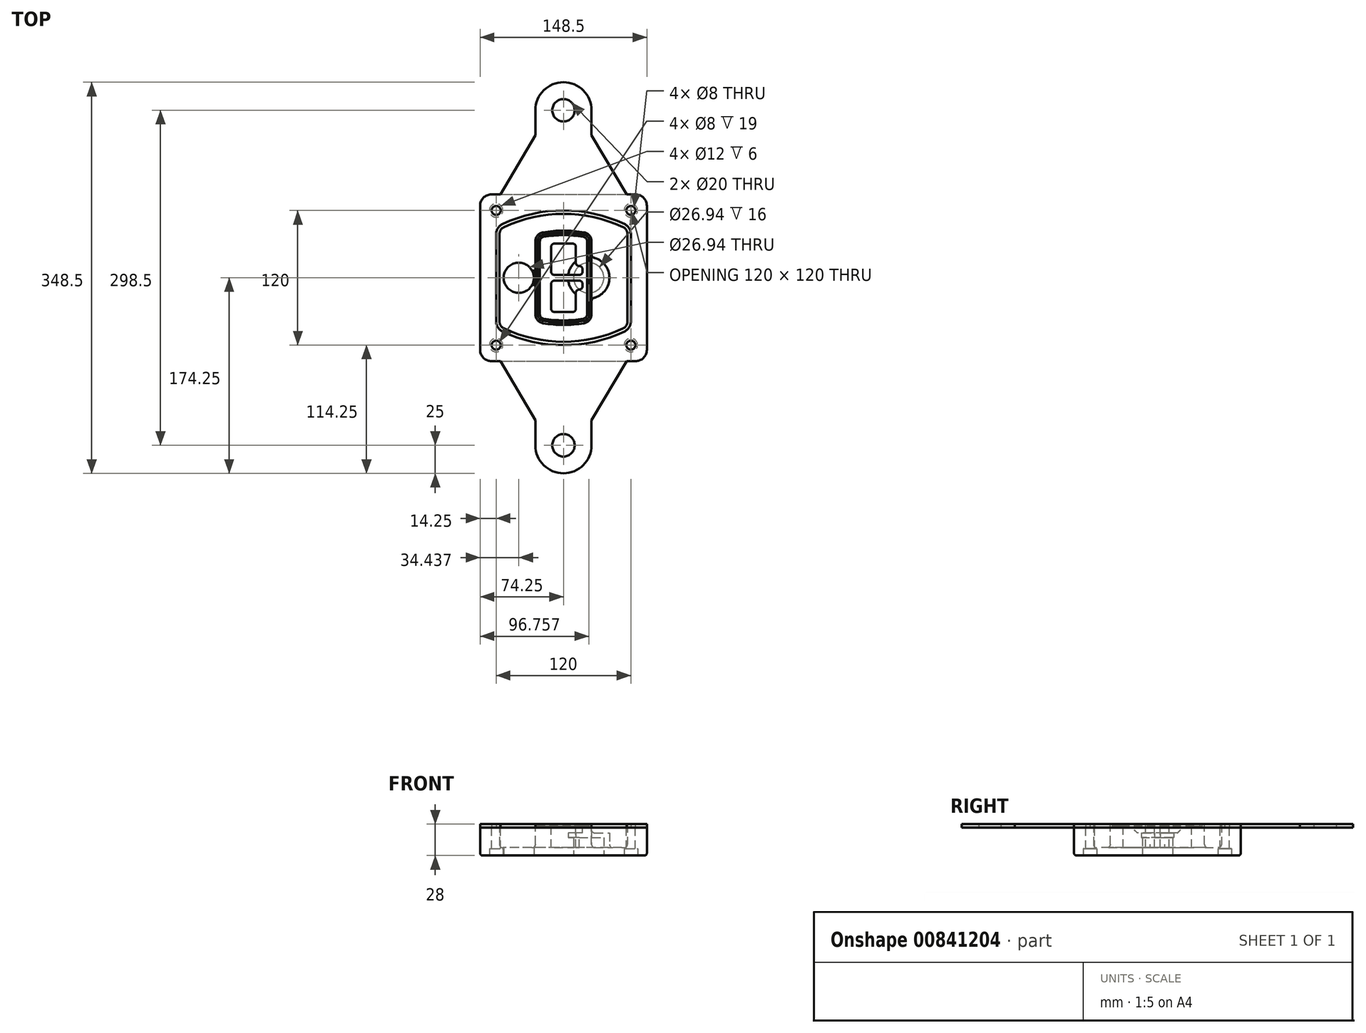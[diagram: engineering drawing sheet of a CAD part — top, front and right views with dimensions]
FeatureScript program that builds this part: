
annotation { "Feature Type Name" : "Feature", "Feature Type Description" : "" }
export const myFeature = defineFeature(function(context is Context, id is Id, definition is map)
    precondition{}
    {
        {
            var Q0;
            Q0=qCreatedBy(makeId("Top.planeOp"),FACE);
            var sketch = newSketch(context, id + "F0", { "sketchPlane" : qUnion([Q0])});
            skPoint(sketch, "E0.rect.middle", {"position": v(0, 0) * mm});
            skLineSegment(sketch, "E1.bottom", {"start": v(-64.25, -74.25) * mm, "end": v(64.25, -74.25) * mm});
            skLineSegment(sketch, "E1.top", {"start": v(-64.25, 74.25) * mm, "end": v(64.25, 74.25) * mm});
            skLineSegment(sketch, "E1.left", {"start": v(-74.25, -64.25) * mm, "end": v(-74.25, 64.25) * mm});
            skLineSegment(sketch, "E1.right", {"start": v(74.25, -64.25) * mm, "end": v(74.25, 64.25) * mm});
            skLineSegment(sketch, "E2", {"start": v(-74.25, 74.25) * mm, "end": v(74.25, -74.25) * mm, "construction": true});
            skLineSegment(sketch, "E3", {"start": v(74.25, 74.25) * mm, "end": v(-74.25, -74.25) * mm, "construction": true});
            skCircle(sketch, "E4", {"center": v(-60, 60) * mm, "radius": 4 * mm});
            skCircle(sketch, "E5", {"center": v(60, 60) * mm, "radius": 4 * mm});
            skCircle(sketch, "E6", {"center": v(60, -60) * mm, "radius": 4 * mm});
            skCircle(sketch, "E7", {"center": v(-60, -60) * mm, "radius": 4 * mm});
            skLineSegment(sketch, "E8", {"start": v(-60, 60) * mm, "end": v(60, 60) * mm, "construction": true});
            skLineSegment(sketch, "E9", {"start": v(60, 60) * mm, "end": v(60, -60) * mm, "construction": true});
            skLineSegment(sketch, "E10", {"start": v(60, -60) * mm, "end": v(-60, -60) * mm, "construction": true});
            skLineSegment(sketch, "E11", {"start": v(-60, -60) * mm, "end": v(-60, 60) * mm, "construction": true});
            skLineSegment(sketch, "E12", {"start": v(-60, 38.83) * mm, "end": v(-60, -38.83) * mm});
            skLineSegment(sketch, "E13", {"start": v(60, 38.83) * mm, "end": v(60, -38.83) * mm});
            skArc(sketch, "E14", {"start": v(54.26, 47.88) * mm, "mid": v(0, 60) * mm, "end": v(-54.26, 47.88) * mm});
            skArc(sketch, "E15", {"start": v(-54.26, -47.88) * mm, "mid": v(0, -60) * mm, "end": v(54.26, -47.88) * mm});
            skLineSegment(sketch, "E16", {"start": v(-60, 0) * mm, "end": v(60, 0) * mm, "construction": true});
            skPoint(sketch, "E17.visualSharp", {"position": v(-60, -45) * mm});
            skArc(sketch, "E17.filletArc", {"start": v(-60, -38.83) * mm, "mid": v(-58.44, -44.2) * mm, "end": v(-54.26, -47.88) * mm});
            skPoint(sketch, "E18.visualSharp", {"position": v(-60, 45) * mm});
            skArc(sketch, "E18.filletArc", {"start": v(-54.26, 47.88) * mm, "mid": v(-58.44, 44.2) * mm, "end": v(-60, 38.83) * mm});
            skPoint(sketch, "E19.visualSharp", {"position": v(60, 45) * mm});
            skArc(sketch, "E19.filletArc", {"start": v(60, 38.83) * mm, "mid": v(58.44, 44.2) * mm, "end": v(54.26, 47.88) * mm});
            skPoint(sketch, "E20.visualSharp", {"position": v(60, -45) * mm});
            skArc(sketch, "E20.filletArc", {"start": v(54.26, -47.88) * mm, "mid": v(58.44, -44.2) * mm, "end": v(60, -38.83) * mm});
            skPoint(sketch, "E21.visualSharp", {"position": v(-74.25, 74.25) * mm});
            skArc(sketch, "E21.filletArc", {"start": v(-64.25, 74.25) * mm, "mid": v(-71.32, 71.32) * mm, "end": v(-74.25, 64.25) * mm});
            skPoint(sketch, "E22.visualSharp", {"position": v(74.25, 74.25) * mm});
            skArc(sketch, "E22.filletArc", {"start": v(74.25, 64.25) * mm, "mid": v(71.32, 71.32) * mm, "end": v(64.25, 74.25) * mm});
            skPoint(sketch, "E23.visualSharp", {"position": v(74.25, -74.25) * mm});
            skArc(sketch, "E23.filletArc", {"start": v(64.25, -74.25) * mm, "mid": v(71.32, -71.32) * mm, "end": v(74.25, -64.25) * mm});
            skPoint(sketch, "E24.visualSharp", {"position": v(-74.25, -74.25) * mm});
            skArc(sketch, "E24.filletArc", {"start": v(-74.25, -64.25) * mm, "mid": v(-71.32, -71.32) * mm, "end": v(-64.25, -74.25) * mm});
            skArc(sketch, "E25.0", {"start": v(57, 38.83) * mm, "mid": v(55.9, 42.58) * mm, "end": v(52.98, 45.17) * mm});
            skLineSegment(sketch, "E25.1", {"start": v(57, 38.83) * mm, "end": v(57, -38.83) * mm});
            skArc(sketch, "E25.2", {"start": v(52.98, -45.17) * mm, "mid": v(55.9, -42.58) * mm, "end": v(57, -38.83) * mm});
            skArc(sketch, "E25.3", {"start": v(-52.98, -45.17) * mm, "mid": v(0, -57) * mm, "end": v(52.98, -45.17) * mm});
            skArc(sketch, "E25.4", {"start": v(-57, -38.83) * mm, "mid": v(-55.9, -42.58) * mm, "end": v(-52.98, -45.17) * mm});
            skArc(sketch, "E25.5", {"start": v(52.98, 45.17) * mm, "mid": v(0, 57) * mm, "end": v(-52.98, 45.17) * mm});
            skLineSegment(sketch, "E25.6", {"start": v(-57, 38.83) * mm, "end": v(-57, -38.83) * mm});
            skArc(sketch, "E25.7", {"start": v(-52.98, 45.17) * mm, "mid": v(-55.9, 42.58) * mm, "end": v(-57, 38.83) * mm});
            skArc(sketch, "E26.0", {"start": v(-55.96, 51.5) * mm, "mid": v(-61.82, 46.33) * mm, "end": v(-64, 38.83) * mm});
            skArc(sketch, "E26.1", {"start": v(55.96, 51.5) * mm, "mid": v(0, 64) * mm, "end": v(-55.96, 51.5) * mm});
            skArc(sketch, "E26.2", {"start": v(64, 38.83) * mm, "mid": v(61.82, 46.33) * mm, "end": v(55.96, 51.5) * mm});
            skLineSegment(sketch, "E26.3", {"start": v(64, 38.83) * mm, "end": v(64, -38.83) * mm});
            skArc(sketch, "E26.4", {"start": v(55.96, -51.5) * mm, "mid": v(61.82, -46.33) * mm, "end": v(64, -38.83) * mm});
            skLineSegment(sketch, "E26.5", {"start": v(-64, 38.83) * mm, "end": v(-64, -38.83) * mm});
            skArc(sketch, "E26.6", {"start": v(-55.96, -51.5) * mm, "mid": v(0, -64) * mm, "end": v(55.96, -51.5) * mm});
            skArc(sketch, "E26.7", {"start": v(-64, -38.83) * mm, "mid": v(-61.82, -46.33) * mm, "end": v(-55.96, -51.5) * mm});
            skSolve(sketch);
        }
        {
            var Q0;
            Q0=makeQuery(id+"F0.imprint","IMPRINT",FACE,{"disambiguationData":[TD([[makeQuery(id+"F0.imprint","IMPRINT",EDGE,{"derivedFrom":sQuery(id+"F0.wireOp",EDGE,"E1.bottom")}),1.0]])]});
            var Q1;
            Q1=makeQuery(id+"F0.imprint","IMPRINT",FACE,{"disambiguationData":[TD([[makeQuery(id+"F0.imprint","IMPRINT",EDGE,{"derivedFrom":sQuery(id+"F0.wireOp",EDGE,"E12")}),1.0]])]});
            var Q2;
            Q2=makeQuery(id+"F0.imprint","IMPRINT",FACE,{"disambiguationData":[TD([[makeQuery(id+"F0.imprint","IMPRINT",EDGE,{"derivedFrom":sQuery(id+"F0.wireOp",EDGE,"E25.0")}),1.0]])]});
            var Q3;
            Q3=makeQuery(id+"F0.imprint","IMPRINT",FACE,{"disambiguationData":[TD([[makeQuery(id+"F0.imprint","IMPRINT",EDGE,{"derivedFrom":sQuery(id+"F0.wireOp",EDGE,"E12")}),-1.0]])]});
            extrude(context, id + "F1", {"entities" : qUnion([Q0, Q1, Q2, Q3]), "oppositeDirection" : true, "depth" : 25 * mm});
        }
        {
            var Q0;
            Q0=makeQuery(id+"F0.imprint","IMPRINT",FACE,{"disambiguationData":[TD([[makeQuery(id+"F0.imprint","IMPRINT",EDGE,{"derivedFrom":sQuery(id+"F0.wireOp",EDGE,"E12")}),1.0]])]});
            extrude(context, id + "F2", {"entities" : qUnion([Q0]), "operationType" : NewBodyOperationType.ADD, "depth" : 3 * mm});
        }
        {
            var Q0;
            Q0=makeQuery(id+"F0.imprint","IMPRINT",FACE,{"disambiguationData":[TD([[makeQuery(id+"F0.imprint","IMPRINT",EDGE,{"derivedFrom":sQuery(id+"F0.wireOp",EDGE,"E25.0")}),1.0]])]});
            extrude(context, id + "F3", {"entities" : qUnion([Q0]), "operationType" : NewBodyOperationType.REMOVE, "oppositeDirection" : true, "depth" : 18 * mm});
        }
        {
            var Q0;
            Q0=makeQuery(id+"F2.opExtrude","CAP_FACE",FACE,{"disambiguationData":[OSD([sQuery(id+"F0.wireOp",EDGE,"E12"),sQuery(id+"F0.wireOp",EDGE,"E13"),sQuery(id+"F0.wireOp",EDGE,"E14"),sQuery(id+"F0.wireOp",EDGE,"E15"),sQuery(id+"F0.wireOp",EDGE,"E17.filletArc"),sQuery(id+"F0.wireOp",EDGE,"E18.filletArc"),sQuery(id+"F0.wireOp",EDGE,"E19.filletArc"),sQuery(id+"F0.wireOp",EDGE,"E20.filletArc"),sQuery(id+"F0.wireOp",EDGE,"E25.0"),sQuery(id+"F0.wireOp",EDGE,"E25.1"),sQuery(id+"F0.wireOp",EDGE,"E25.2"),sQuery(id+"F0.wireOp",EDGE,"E25.3"),sQuery(id+"F0.wireOp",EDGE,"E25.4"),sQuery(id+"F0.wireOp",EDGE,"E25.5"),sQuery(id+"F0.wireOp",EDGE,"E25.6"),sQuery(id+"F0.wireOp",EDGE,"E25.7")])],"isStart":false});
            var sketch = newSketch(context, id + "F4", { "sketchPlane" : qUnion([Q0])});
            skArc(sketch, "E27.0", {"start": v(-18.34, -40.45) * mm, "mid": v(0, -42) * mm, "end": v(18.34, -40.45) * mm});
            skArc(sketch, "E28.0", {"start": v(18.34, 40.45) * mm, "mid": v(0, 42) * mm, "end": v(-18.34, 40.45) * mm});
            skLineSegment(sketch, "E29", {"start": v(-25, 32.57) * mm, "end": v(-25, -32.57) * mm});
            skLineSegment(sketch, "E30", {"start": v(25, 32.57) * mm, "end": v(25, -32.57) * mm});
            skLineSegment(sketch, "E31", {"start": v(-25, 39.1) * mm, "end": v(25, 39.1) * mm, "construction": true});
            skLineSegment(sketch, "E32", {"start": v(-25, -39.1) * mm, "end": v(25, -39.1) * mm, "construction": true});
            skPoint(sketch, "E33.visualSharp", {"position": v(-25, 39.1) * mm});
            skArc(sketch, "E33.filletArc", {"start": v(-18.34, 40.45) * mm, "mid": v(-23.11, 37.73) * mm, "end": v(-25, 32.57) * mm});
            skPoint(sketch, "E34.visualSharp", {"position": v(25, 39.1) * mm});
            skArc(sketch, "E34.filletArc", {"start": v(25, 32.57) * mm, "mid": v(23.11, 37.73) * mm, "end": v(18.34, 40.45) * mm});
            skPoint(sketch, "E35.visualSharp", {"position": v(25, -39.1) * mm});
            skArc(sketch, "E35.filletArc", {"start": v(18.34, -40.45) * mm, "mid": v(23.11, -37.73) * mm, "end": v(25, -32.57) * mm});
            skPoint(sketch, "E36.visualSharp", {"position": v(-25, -39.1) * mm});
            skArc(sketch, "E36.filletArc", {"start": v(-25, -32.57) * mm, "mid": v(-23.11, -37.73) * mm, "end": v(-18.34, -40.45) * mm});
            skArc(sketch, "E37.0", {"start": v(52.98, 45.17) * mm, "mid": v(0, 57) * mm, "end": v(-52.98, 45.17) * mm});
            skArc(sketch, "E37.1", {"start": v(-52.98, 45.17) * mm, "mid": v(-55.9, 42.58) * mm, "end": v(-57, 38.83) * mm});
            skLineSegment(sketch, "E37.2", {"start": v(-57, 38.83) * mm, "end": v(-57, -38.83) * mm});
            skArc(sketch, "E37.3", {"start": v(-57, -38.83) * mm, "mid": v(-55.9, -42.58) * mm, "end": v(-52.98, -45.17) * mm});
            skArc(sketch, "E37.4", {"start": v(-52.98, -45.17) * mm, "mid": v(0, -57) * mm, "end": v(52.98, -45.17) * mm});
            skArc(sketch, "E37.5", {"start": v(52.98, -45.17) * mm, "mid": v(55.9, -42.58) * mm, "end": v(57, -38.83) * mm});
            skLineSegment(sketch, "E37.6", {"start": v(57, 38.83) * mm, "end": v(57, -38.83) * mm});
            skArc(sketch, "E37.7", {"start": v(57, 38.83) * mm, "mid": v(55.9, 42.58) * mm, "end": v(52.98, 45.17) * mm});
            skLineSegment(sketch, "E38.0", {"start": v(23, 32.57) * mm, "end": v(23, -32.57) * mm});
            skArc(sketch, "E38.1", {"start": v(18, -38.48) * mm, "mid": v(21.58, -36.44) * mm, "end": v(23, -32.57) * mm});
            skArc(sketch, "E38.2", {"start": v(-18, -38.48) * mm, "mid": v(0, -40) * mm, "end": v(18, -38.48) * mm});
            skArc(sketch, "E38.3", {"start": v(-23, -32.57) * mm, "mid": v(-21.58, -36.44) * mm, "end": v(-18, -38.48) * mm});
            skLineSegment(sketch, "E38.4", {"start": v(-23, 32.57) * mm, "end": v(-23, -32.57) * mm});
            skArc(sketch, "E38.5", {"start": v(23, 32.57) * mm, "mid": v(21.58, 36.44) * mm, "end": v(18, 38.48) * mm});
            skArc(sketch, "E38.6", {"start": v(-18, 38.48) * mm, "mid": v(-21.58, 36.44) * mm, "end": v(-23, 32.57) * mm});
            skArc(sketch, "E38.7", {"start": v(18, 38.48) * mm, "mid": v(0, 40) * mm, "end": v(-18, 38.48) * mm});
            skArc(sketch, "E39.0", {"start": v(21, 32.57) * mm, "mid": v(20.06, 35.15) * mm, "end": v(17.67, 36.5) * mm});
            skLineSegment(sketch, "E39.1", {"start": v(21, 32.57) * mm, "end": v(21, -32.57) * mm});
            skArc(sketch, "E39.2", {"start": v(17.67, -36.5) * mm, "mid": v(20.06, -35.15) * mm, "end": v(21, -32.57) * mm});
            skArc(sketch, "E39.3", {"start": v(-17.67, -36.5) * mm, "mid": v(0, -38) * mm, "end": v(17.67, -36.5) * mm});
            skArc(sketch, "E39.4", {"start": v(-21, -32.57) * mm, "mid": v(-20.06, -35.15) * mm, "end": v(-17.67, -36.5) * mm});
            skArc(sketch, "E39.5", {"start": v(17.67, 36.5) * mm, "mid": v(0, 38) * mm, "end": v(-17.67, 36.5) * mm});
            skLineSegment(sketch, "E39.6", {"start": v(-21, 32.57) * mm, "end": v(-21, -32.57) * mm});
            skArc(sketch, "E39.7", {"start": v(-17.67, 36.5) * mm, "mid": v(-20.06, 35.15) * mm, "end": v(-21, 32.57) * mm});
            skLineSegment(sketch, "E40", {"start": v(-25, 0) * mm, "end": v(25, 0) * mm, "construction": true});
            skLineSegment(sketch, "E41", {"start": v(-11, 5.5) * mm, "end": v(-11, 27.5) * mm});
            skLineSegment(sketch, "E42", {"start": v(-8, 30.5) * mm, "end": v(8, 30.5) * mm});
            skLineSegment(sketch, "E43", {"start": v(11, 27.5) * mm, "end": v(11, 13.5) * mm});
            skLineSegment(sketch, "E44", {"start": v(14, 10.5) * mm, "end": v(14, 10.5) * mm});
            skLineSegment(sketch, "E45", {"start": v(17, 7.5) * mm, "end": v(17, 5.5) * mm});
            skLineSegment(sketch, "E46", {"start": v(14, 2.5) * mm, "end": v(-8, 2.5) * mm});
            skPoint(sketch, "E47.visualSharp", {"position": v(-11, 30.5) * mm});
            skArc(sketch, "E47.filletArc", {"start": v(-8, 30.5) * mm, "mid": v(-10.12, 29.62) * mm, "end": v(-11, 27.5) * mm});
            skPoint(sketch, "E48.visualSharp", {"position": v(11, 30.5) * mm});
            skArc(sketch, "E48.filletArc", {"start": v(11, 27.5) * mm, "mid": v(10.12, 29.62) * mm, "end": v(8, 30.5) * mm});
            skPoint(sketch, "E49.visualSharp", {"position": v(11, 10.5) * mm});
            skArc(sketch, "E49.filletArc", {"start": v(11, 13.5) * mm, "mid": v(11.88, 11.38) * mm, "end": v(14, 10.5) * mm});
            skPoint(sketch, "E50.visualSharp", {"position": v(17, 10.5) * mm});
            skArc(sketch, "E50.filletArc", {"start": v(17, 7.5) * mm, "mid": v(16.12, 9.62) * mm, "end": v(14, 10.5) * mm});
            skPoint(sketch, "E51.visualSharp", {"position": v(17, 2.5) * mm});
            skArc(sketch, "E51.filletArc", {"start": v(14, 2.5) * mm, "mid": v(16.12, 3.38) * mm, "end": v(17, 5.5) * mm});
            skPoint(sketch, "E52.visualSharp", {"position": v(-11, 2.5) * mm});
            skArc(sketch, "E52.filletArc", {"start": v(-11, 5.5) * mm, "mid": v(-10.12, 3.38) * mm, "end": v(-8, 2.5) * mm});
            skLineSegment(sketch, "E53.0.MirrorCS", {"start": v(14, -2.5) * mm, "end": v(-8, -2.5) * mm});
            skArc(sketch, "E54.0.MirrorCS", {"start": v(-11, -5.5) * mm, "mid": v(-10.12, -3.38) * mm, "end": v(-8, -2.5) * mm});
            skLineSegment(sketch, "E55.0.MirrorCS", {"start": v(-11, -5.5) * mm, "end": v(-11, -27.5) * mm});
            skArc(sketch, "E56.0.MirrorCS", {"start": v(-8, -30.5) * mm, "mid": v(-10.12, -29.62) * mm, "end": v(-11, -27.5) * mm});
            skLineSegment(sketch, "E57.0.MirrorCS", {"start": v(-8, -30.5) * mm, "end": v(8, -30.5) * mm});
            skArc(sketch, "E58.0.MirrorCS", {"start": v(11, -27.5) * mm, "mid": v(10.12, -29.62) * mm, "end": v(8, -30.5) * mm});
            skLineSegment(sketch, "E59.0.MirrorCS", {"start": v(11, -27.5) * mm, "end": v(11, -13.5) * mm});
            skArc(sketch, "E60.0.MirrorCS", {"start": v(11, -13.5) * mm, "mid": v(11.88, -11.38) * mm, "end": v(14, -10.5) * mm});
            skArc(sketch, "E61.0.MirrorCS", {"start": v(17, -7.5) * mm, "mid": v(16.12, -9.62) * mm, "end": v(14, -10.5) * mm});
            skLineSegment(sketch, "E62.0.MirrorCS", {"start": v(17, -7.5) * mm, "end": v(17, -5.5) * mm});
            skArc(sketch, "E63.0.MirrorCS", {"start": v(14, -2.5) * mm, "mid": v(16.12, -3.38) * mm, "end": v(17, -5.5) * mm});
            skSolve(sketch);
        }
        {
            var Q0;
            Q0=makeQuery(id+"F4.imprint","IMPRINT",FACE,{"disambiguationData":[TD([[makeQuery(id+"F4.imprint","IMPRINT",EDGE,{"derivedFrom":sQuery(id+"F4.wireOp",EDGE,"E27.0")}),1.0]])]});
            var Q1;
            Q1=makeQuery(id+"F4.imprint","IMPRINT",FACE,{"disambiguationData":[TD([[makeQuery(id+"F4.imprint","IMPRINT",EDGE,{"derivedFrom":sQuery(id+"F4.wireOp",EDGE,"E38.0")}),-1.0]])]});
            var Q2;
            Q2=makeQuery(id+"F4.imprint","IMPRINT",FACE,{"disambiguationData":[TD([[makeQuery(id+"F4.imprint","IMPRINT",EDGE,{"derivedFrom":sQuery(id+"F4.wireOp",EDGE,"E39.0")}),1.0]])]});
            extrude(context, id + "F5", {"entities" : qUnion([Q0, Q1, Q2]), "operationType" : NewBodyOperationType.ADD, "endBound" : BoundingType.UP_TO_NEXT, "oppositeDirection" : true, "depth" : 25 * mm});
        }
        {
            var Q0;
            Q0=makeQuery(id+"F4.imprint","IMPRINT",FACE,{"disambiguationData":[TD([[makeQuery(id+"F4.imprint","IMPRINT",EDGE,{"derivedFrom":sQuery(id+"F4.wireOp",EDGE,"E38.0")}),-1.0]])]});
            extrude(context, id + "F6", {"entities" : qUnion([Q0]), "operationType" : NewBodyOperationType.REMOVE, "oppositeDirection" : true, "depth" : 2 * mm});
        }
        {
            var Q0;
            Q0=makeQuery(id+"F1.opExtrude","CAP_FACE",FACE,{"disambiguationData":[OSD([sQuery(id+"F0.wireOp",EDGE,"E1.bottom"),sQuery(id+"F0.wireOp",EDGE,"E1.top"),sQuery(id+"F0.wireOp",EDGE,"E1.left"),sQuery(id+"F0.wireOp",EDGE,"E1.right"),sQuery(id+"F0.wireOp",EDGE,"E4"),sQuery(id+"F0.wireOp",EDGE,"E5"),sQuery(id+"F0.wireOp",EDGE,"E6"),sQuery(id+"F0.wireOp",EDGE,"E7"),sQuery(id+"F0.wireOp",EDGE,"E21.filletArc"),sQuery(id+"F0.wireOp",EDGE,"E22.filletArc"),sQuery(id+"F0.wireOp",EDGE,"E23.filletArc"),sQuery(id+"F0.wireOp",EDGE,"E24.filletArc")])],"isStart":false});
            var sketch = newSketch(context, id + "F7", { "sketchPlane" : qUnion([Q0])});
            skCircle(sketch, "E64", {"center": v(22.5, 0) * mm, "radius": 13.47 * mm});
            skCircle(sketch, "E65", {"center": v(-39.81, 0) * mm, "radius": 13.47 * mm});
            skLineSegment(sketch, "E66", {"start": v(74.25, 0) * mm, "end": v(-74.25, 0) * mm});
            skCircle(sketch, "E67", {"center": v(22.5, 0) * mm, "radius": 18.47 * mm});
            skCircle(sketch, "E68", {"center": v(60, -60) * mm, "radius": 6 * mm});
            skCircle(sketch, "E69", {"center": v(-60, -60) * mm, "radius": 6 * mm});
            skCircle(sketch, "E70", {"center": v(-60, 60) * mm, "radius": 6 * mm});
            skCircle(sketch, "E71", {"center": v(60, 60) * mm, "radius": 6 * mm});
            skSolve(sketch);
        }
        {
            var Q0;
            {var subQ1=sQuery(id+"F7.wireOp",EDGE,"E66");var subQ4=sQuery(id+"F7.wireOp",EDGE,"E64");var subQ6=makeQuery(id+"F7.imprint","INTERSECT",VERTEX,{"disambiguationData":[OD(0.0)],"derivedFrom":[subQ4,subQ1]});Q0=makeQuery(id+"F7.imprint","IMPRINT",FACE,{"disambiguationData":[TD([[makeQuery(id+"F7.imprint","IMPRINT",EDGE,{"disambiguationData":[TD([[subQ6,-1.0]])],"derivedFrom":subQ4}),-1.0]])]});}
            var Q1;
            {var subQ0=sQuery(id+"F7.wireOp",EDGE,"E66");var subQ1=sQuery(id+"F7.wireOp",EDGE,"E64");var subQ3=makeQuery(id+"F7.imprint","INTERSECT",VERTEX,{"disambiguationData":[OD(0.0)],"derivedFrom":[subQ1,subQ0]});Q1=makeQuery(id+"F7.imprint","IMPRINT",FACE,{"disambiguationData":[TD([[makeQuery(id+"F7.imprint","IMPRINT",EDGE,{"disambiguationData":[TD([[subQ3,-1.0]])],"derivedFrom":subQ1}),1.0]])]});}
            var Q2;
            {var subQ0=sQuery(id+"F7.wireOp",EDGE,"E66");var subQ1=sQuery(id+"F7.wireOp",EDGE,"E64");var subQ3=makeQuery(id+"F7.imprint","INTERSECT",VERTEX,{"disambiguationData":[OD(0.0)],"derivedFrom":[subQ1,subQ0]});Q2=makeQuery(id+"F7.imprint","IMPRINT",FACE,{"disambiguationData":[TD([[makeQuery(id+"F7.imprint","IMPRINT",EDGE,{"disambiguationData":[TD([[subQ3,1.0]])],"derivedFrom":subQ1}),1.0]])]});}
            var Q3;
            {var subQ1=sQuery(id+"F7.wireOp",EDGE,"E66");var subQ4=sQuery(id+"F7.wireOp",EDGE,"E64");var subQ6=makeQuery(id+"F7.imprint","INTERSECT",VERTEX,{"disambiguationData":[OD(0.0)],"derivedFrom":[subQ4,subQ1]});Q3=makeQuery(id+"F7.imprint","IMPRINT",FACE,{"disambiguationData":[TD([[makeQuery(id+"F7.imprint","IMPRINT",EDGE,{"disambiguationData":[TD([[subQ6,1.0]])],"derivedFrom":subQ4}),-1.0]])]});}
            extrude(context, id + "F8", {"entities" : qUnion([Q0, Q1, Q2, Q3]), "operationType" : NewBodyOperationType.ADD, "oppositeDirection" : true, "depth" : 20 * mm});
        }
        {
            var Q0;
            {var subQ0=sQuery(id+"F7.wireOp",EDGE,"E66");var subQ1=sQuery(id+"F7.wireOp",EDGE,"E64");var subQ3=makeQuery(id+"F7.imprint","INTERSECT",VERTEX,{"disambiguationData":[OD(0.0)],"derivedFrom":[subQ1,subQ0]});Q0=makeQuery(id+"F7.imprint","IMPRINT",FACE,{"disambiguationData":[TD([[makeQuery(id+"F7.imprint","IMPRINT",EDGE,{"disambiguationData":[TD([[subQ3,-1.0]])],"derivedFrom":subQ1}),1.0]])]});}
            var Q1;
            {var subQ0=sQuery(id+"F7.wireOp",EDGE,"E66");var subQ1=sQuery(id+"F7.wireOp",EDGE,"E64");var subQ3=makeQuery(id+"F7.imprint","INTERSECT",VERTEX,{"disambiguationData":[OD(0.0)],"derivedFrom":[subQ1,subQ0]});Q1=makeQuery(id+"F7.imprint","IMPRINT",FACE,{"disambiguationData":[TD([[makeQuery(id+"F7.imprint","IMPRINT",EDGE,{"disambiguationData":[TD([[subQ3,1.0]])],"derivedFrom":subQ1}),1.0]])]});}
            extrude(context, id + "F9", {"entities" : qUnion([Q0, Q1]), "operationType" : NewBodyOperationType.REMOVE, "oppositeDirection" : true, "depth" : 16 * mm});
        }
        {
            var Q0;
            {var subQ0=sQuery(id+"F7.wireOp",EDGE,"E66");var subQ1=sQuery(id+"F7.wireOp",EDGE,"E65");var subQ3=makeQuery(id+"F7.imprint","INTERSECT",VERTEX,{"disambiguationData":[OD(0.0)],"derivedFrom":[subQ1,subQ0]});Q0=makeQuery(id+"F7.imprint","IMPRINT",FACE,{"disambiguationData":[TD([[makeQuery(id+"F7.imprint","IMPRINT",EDGE,{"disambiguationData":[TD([[subQ3,-1.0]])],"derivedFrom":subQ1}),1.0]])]});}
            var Q1;
            {var subQ0=sQuery(id+"F7.wireOp",EDGE,"E66");var subQ1=sQuery(id+"F7.wireOp",EDGE,"E65");var subQ3=makeQuery(id+"F7.imprint","INTERSECT",VERTEX,{"disambiguationData":[OD(0.0)],"derivedFrom":[subQ1,subQ0]});Q1=makeQuery(id+"F7.imprint","IMPRINT",FACE,{"disambiguationData":[TD([[makeQuery(id+"F7.imprint","IMPRINT",EDGE,{"disambiguationData":[TD([[subQ3,1.0]])],"derivedFrom":subQ1}),1.0]])]});}
            extrude(context, id + "F10", {"entities" : qUnion([Q0, Q1]), "operationType" : NewBodyOperationType.REMOVE, "oppositeDirection" : true, "depth" : 25 * mm});
        }
        {
            var Q0;
            Q0=makeQuery(id+"F7.imprint","IMPRINT",FACE,{"disambiguationData":[TD([[makeQuery(id+"F7.imprint","IMPRINT",EDGE,{"derivedFrom":sQuery(id+"F7.wireOp",EDGE,"E68")}),1.0]])]});
            var Q1;
            Q1=makeQuery(id+"F7.imprint","IMPRINT",FACE,{"disambiguationData":[TD([[makeQuery(id+"F7.imprint","IMPRINT",EDGE,{"derivedFrom":makeQuery(id+"F1.opExtrude","CAP_EDGE",EDGE,{"disambiguationData":[OSD([sQuery(id+"F0.wireOp",EDGE,"E5")])],"isStart":false})}),-1.0]])]});
            var Q2;
            Q2=makeQuery(id+"F7.imprint","IMPRINT",FACE,{"disambiguationData":[TD([[makeQuery(id+"F7.imprint","IMPRINT",EDGE,{"derivedFrom":sQuery(id+"F7.wireOp",EDGE,"E69")}),1.0]])]});
            var Q3;
            Q3=makeQuery(id+"F7.imprint","IMPRINT",FACE,{"disambiguationData":[TD([[makeQuery(id+"F7.imprint","IMPRINT",EDGE,{"derivedFrom":makeQuery(id+"F1.opExtrude","CAP_EDGE",EDGE,{"disambiguationData":[OSD([sQuery(id+"F0.wireOp",EDGE,"E4")])],"isStart":false})}),-1.0]])]});
            var Q4;
            Q4=makeQuery(id+"F7.imprint","IMPRINT",FACE,{"disambiguationData":[TD([[makeQuery(id+"F7.imprint","IMPRINT",EDGE,{"derivedFrom":sQuery(id+"F7.wireOp",EDGE,"E70")}),1.0]])]});
            var Q5;
            Q5=makeQuery(id+"F7.imprint","IMPRINT",FACE,{"disambiguationData":[TD([[makeQuery(id+"F7.imprint","IMPRINT",EDGE,{"derivedFrom":makeQuery(id+"F1.opExtrude","CAP_EDGE",EDGE,{"disambiguationData":[OSD([sQuery(id+"F0.wireOp",EDGE,"E7")])],"isStart":false})}),-1.0]])]});
            var Q6;
            Q6=makeQuery(id+"F7.imprint","IMPRINT",FACE,{"disambiguationData":[TD([[makeQuery(id+"F7.imprint","IMPRINT",EDGE,{"derivedFrom":sQuery(id+"F7.wireOp",EDGE,"E71")}),1.0]])]});
            var Q7;
            Q7=makeQuery(id+"F7.imprint","IMPRINT",FACE,{"disambiguationData":[TD([[makeQuery(id+"F7.imprint","IMPRINT",EDGE,{"derivedFrom":makeQuery(id+"F1.opExtrude","CAP_EDGE",EDGE,{"disambiguationData":[OSD([sQuery(id+"F0.wireOp",EDGE,"E6")])],"isStart":false})}),-1.0]])]});
            extrude(context, id + "F11", {"entities" : qUnion([Q0, Q1, Q2, Q3, Q4, Q5, Q6, Q7]), "operationType" : NewBodyOperationType.REMOVE, "oppositeDirection" : true, "depth" : 6 * mm});
        }
        {
            var Q0;
            Q0=makeQuery(id+"F9.boolean.opBoolean","COPY",FACE,{"derivedFrom":makeQuery(id+"F9.opExtrude","CAP_FACE",FACE,{"disambiguationData":[OSD([sQuery(id+"F7.wireOp",EDGE,"E64")])],"isStart":false})});
            var sketch = newSketch(context, id + "F12", { "sketchPlane" : qUnion([Q0])});
            skArc(sketch, "E72.0", {"start": v(11, 14.45) * mm, "mid": v(6.45, 9.13) * mm, "end": v(4.2, 2.5) * mm});
            skArc(sketch, "E72.1", {"start": v(4.2, -2.5) * mm, "mid": v(6.45, -9.13) * mm, "end": v(11, -14.45) * mm});
            skLineSegment(sketch, "E73", {"start": v(4.2, -2.5) * mm, "end": v(14, -2.5) * mm});
            skLineSegment(sketch, "E74.0", {"start": v(14, 2.5) * mm, "end": v(4.2, 2.5) * mm});
            skArc(sketch, "E74.1", {"start": v(14, 2.5) * mm, "mid": v(16.12, 3.38) * mm, "end": v(17, 5.5) * mm});
            skLineSegment(sketch, "E74.2", {"start": v(17, 7.5) * mm, "end": v(17, 5.5) * mm});
            skArc(sketch, "E74.3", {"start": v(17, 7.5) * mm, "mid": v(16.12, 9.62) * mm, "end": v(14, 10.5) * mm});
            skArc(sketch, "E74.4", {"start": v(11, 13.5) * mm, "mid": v(11.88, 11.38) * mm, "end": v(14, 10.5) * mm});
            skLineSegment(sketch, "E74.5", {"start": v(11, 14.45) * mm, "end": v(11, 13.5) * mm});
            skLineSegment(sketch, "E74.7", {"start": v(14, -2.5) * mm, "end": v(4.2, -2.5) * mm});
            skArc(sketch, "E74.8", {"start": v(14, -2.5) * mm, "mid": v(16.12, -3.38) * mm, "end": v(17, -5.5) * mm});
            skLineSegment(sketch, "E74.9", {"start": v(17, -7.5) * mm, "end": v(17, -5.5) * mm});
            skArc(sketch, "E74.10", {"start": v(17, -7.5) * mm, "mid": v(16.12, -9.62) * mm, "end": v(14, -10.5) * mm});
            skArc(sketch, "E74.11", {"start": v(11, -13.5) * mm, "mid": v(11.88, -11.38) * mm, "end": v(14, -10.5) * mm});
            skLineSegment(sketch, "E74.12", {"start": v(11, -14.45) * mm, "end": v(11, -13.5) * mm});
            skPoint(sketch, "E75.orphan", {"position": v(11, -27.5) * mm});
            skPoint(sketch, "E76.orphan", {"position": v(-8, -2.5) * mm});
            skPoint(sketch, "E77.orphan", {"position": v(-8, 2.5) * mm});
            skPoint(sketch, "E78.orphan", {"position": v(11, 27.5) * mm});
            skSolve(sketch);
        }
        {
            var Q0;
            {var subQ7=sQuery(id+"F12.wireOp",EDGE,"E72.0");var subQ14=sQuery(id+"F12.wireOp",EDGE,"E72.1");var subQ16=sQuery(id+"F12.wireOp",EDGE,"E74.1");var subQ18=sQuery(id+"F12.wireOp",EDGE,"E74.8");Q0=qUnion([makeQuery(id+"F12.imprint","IMPRINT",FACE,{"disambiguationData":[TD([[makeQuery(id+"F12.imprint","IMPRINT",EDGE,{"derivedFrom":subQ7}),1.0]])]}),makeQuery(id+"F12.imprint","IMPRINT",FACE,{"disambiguationData":[TD([[makeQuery(id+"F12.imprint","IMPRINT",EDGE,{"derivedFrom":subQ14}),1.0]])]}),makeQuery(id+"F12.imprint","IMPRINT",FACE,{"disambiguationData":[TD([[makeQuery(id+"F12.imprint","IMPRINT",EDGE,{"derivedFrom":subQ16}),1.0]])]}),makeQuery(id+"F12.imprint","IMPRINT",FACE,{"disambiguationData":[TD([[makeQuery(id+"F12.imprint","IMPRINT",EDGE,{"derivedFrom":subQ18}),-1.0]])]})]);}
            var Q1;
            Q1=makeQuery(id+"F5.boolean.opBoolean","SPLIT",FACE,{"disambiguationData":[TD([makeQuery(id+"F5.opExtrude","SWEPT_FACE",FACE,{"disambiguationData":[OSD([sQuery(id+"F4.wireOp",EDGE,"E41")])]})])],"derivedFrom":makeQuery(id+"F3.boolean.opBoolean","COPY",FACE,{"derivedFrom":makeQuery(id+"F3.opExtrude","CAP_FACE",FACE,{"disambiguationData":[OSD([sQuery(id+"F0.wireOp",EDGE,"E25.0"),sQuery(id+"F0.wireOp",EDGE,"E25.1"),sQuery(id+"F0.wireOp",EDGE,"E25.2"),sQuery(id+"F0.wireOp",EDGE,"E25.3"),sQuery(id+"F0.wireOp",EDGE,"E25.4"),sQuery(id+"F0.wireOp",EDGE,"E25.5"),sQuery(id+"F0.wireOp",EDGE,"E25.6"),sQuery(id+"F0.wireOp",EDGE,"E25.7")])],"isStart":false})})});
            extrude(context, id + "F13", {"entities" : qUnion([Q0]), "operationType" : NewBodyOperationType.REMOVE, "endBound" : BoundingType.UP_TO_SURFACE, "endBoundEntityFace" : qUnion([Q1]), "depth" : 25 * mm});
        }
        {
            var Q0;
            Q0=makeQuery(id+"F3.boolean.opBoolean","COPY",EDGE,{"derivedFrom":makeQuery(id+"F3.opExtrude","CAP_EDGE",EDGE,{"disambiguationData":[OSD([sQuery(id+"F0.wireOp",EDGE,"E25.6")])],"isStart":false})});
            var Q1;
            Q1=makeQuery(id+"F8.boolean.opBoolean","INTERSECT",EDGE,{"derivedFrom":[makeQuery(id+"F5.opExtrude","SWEPT_FACE",FACE,{"disambiguationData":[OSD([sQuery(id+"F4.wireOp",EDGE,"E30")])]}),makeQuery(id+"F8.opExtrude","CAP_FACE",FACE,{"disambiguationData":[OSD([sQuery(id+"F7.wireOp",EDGE,"E67")])],"isStart":false})]});
            var Q2;
            Q2=makeQuery(id+"F8.boolean.opBoolean","INTERSECT",EDGE,{"disambiguationData":[OD(1.0)],"derivedFrom":[makeQuery(id+"F5.opExtrude","SWEPT_FACE",FACE,{"disambiguationData":[OSD([sQuery(id+"F4.wireOp",EDGE,"E30")])]}),makeQuery(id+"F8.opExtrude","SWEPT_FACE",FACE,{"disambiguationData":[OSD([sQuery(id+"F7.wireOp",EDGE,"E67")])]})]});
            var Q3;
            {var subQ0=sQuery(id+"F4.wireOp",EDGE,"E30");Q3=makeQuery(id+"F8.boolean.opBoolean","SPLIT",EDGE,{"disambiguationData":[TD([makeQuery(id+"F5.opExtrude","SWEPT_FACE",FACE,{"disambiguationData":[OSD([sQuery(id+"F4.wireOp",EDGE,"E35.filletArc")])]})])],"derivedFrom":makeQuery(id+"F5.opExtrude","CAP_EDGE",EDGE,{"disambiguationData":[OSD([subQ0])],"isStart":false})});}
            var Q4;
            {var subQ0=sQuery(id+"F0.wireOp",EDGE,"E25.7");var subQ1=sQuery(id+"F0.wireOp",EDGE,"E25.1");var subQ2=sQuery(id+"F0.wireOp",EDGE,"E25.6");var subQ3=sQuery(id+"F0.wireOp",EDGE,"E25.5");var subQ4=sQuery(id+"F0.wireOp",EDGE,"E25.4");var subQ5=sQuery(id+"F0.wireOp",EDGE,"E25.0");var subQ6=sQuery(id+"F0.wireOp",EDGE,"E25.2");var subQ7=sQuery(id+"F0.wireOp",EDGE,"E25.3");Q4=makeQuery(id+"F8.boolean.opBoolean","INTERSECT",EDGE,{"derivedFrom":[makeQuery(id+"F5.boolean.opBoolean","SPLIT",FACE,{"disambiguationData":[TD([makeQuery(id+"F2.opExtrude","SWEPT_FACE",FACE,{"disambiguationData":[OSD([subQ5])]})])],"derivedFrom":makeQuery(id+"F3.boolean.opBoolean","COPY",FACE,{"derivedFrom":makeQuery(id+"F3.opExtrude","CAP_FACE",FACE,{"disambiguationData":[OSD([subQ5,subQ1,subQ6,subQ7,subQ4,subQ3,subQ2,subQ0])],"isStart":false})})}),makeQuery(id+"F8.opExtrude","SWEPT_FACE",FACE,{"disambiguationData":[OSD([sQuery(id+"F7.wireOp",EDGE,"E67")])]})]});}
            var Q5;
            Q5=makeQuery(id+"F8.boolean.opBoolean","INTERSECT",EDGE,{"disambiguationData":[OD(0.0)],"derivedFrom":[makeQuery(id+"F5.opExtrude","SWEPT_FACE",FACE,{"disambiguationData":[OSD([sQuery(id+"F4.wireOp",EDGE,"E30")])]}),makeQuery(id+"F8.opExtrude","SWEPT_FACE",FACE,{"disambiguationData":[OSD([sQuery(id+"F7.wireOp",EDGE,"E67")])]})]});
            fillet(context, id + "F14", {"entities" : qUnion([Q0, Q1, Q2, Q3, Q4, Q5]), "radius" : 3 * mm, "tangentPropagation" : true, "allowEdgeOverflow" : false});
        }
        {
            var Q0;
            Q0=makeQuery(id+"F1.opExtrude","CAP_EDGE",EDGE,{"disambiguationData":[OSD([sQuery(id+"F0.wireOp",EDGE,"E1.bottom")])],"isStart":false});
            fillet(context, id + "F15", {"entities" : qUnion([Q0]), "radius" : 2 * mm, "tangentPropagation" : true, "allowEdgeOverflow" : false});
        }
        {
            var Q0;
            {var subQ0=sQuery(id+"F0.wireOp",EDGE,"E21.filletArc");var subQ1=sQuery(id+"F0.wireOp",EDGE,"E7");var subQ2=sQuery(id+"F0.wireOp",EDGE,"E6");var subQ3=sQuery(id+"F0.wireOp",EDGE,"E5");var subQ4=sQuery(id+"F0.wireOp",EDGE,"E4");var subQ5=sQuery(id+"F0.wireOp",EDGE,"E22.filletArc");var subQ6=sQuery(id+"F0.wireOp",EDGE,"E1.bottom");var subQ7=sQuery(id+"F0.wireOp",EDGE,"E1.right");var subQ8=sQuery(id+"F0.wireOp",EDGE,"E1.top");var subQ9=sQuery(id+"F0.wireOp",EDGE,"E1.left");var subQ10=sQuery(id+"F0.wireOp",EDGE,"E23.filletArc");var subQ11=sQuery(id+"F0.wireOp",EDGE,"E24.filletArc");Q0=makeQuery(id+"F2.boolean.opBoolean","SPLIT",FACE,{"disambiguationData":[TD([makeQuery(id+"F1.opExtrude","SWEPT_FACE",FACE,{"disambiguationData":[OSD([subQ6])]})])],"derivedFrom":makeQuery(id+"F1.opExtrude","CAP_FACE",FACE,{"disambiguationData":[OSD([subQ6,subQ8,subQ9,subQ7,subQ4,subQ3,subQ2,subQ1,subQ0,subQ5,subQ10,subQ11])],"isStart":true})});}
            var sketch = newSketch(context, id + "F16", { "sketchPlane" : qUnion([Q0])});
            skLineSegment(sketch, "E79", {"start": v(0, 74.25) * mm, "end": v(0, 149.25) * mm, "construction": true});
            skCircle(sketch, "E80", {"center": v(0, 149.25) * mm, "radius": 10 * mm});
            skArc(sketch, "E81", {"start": v(-25, 149.25) * mm, "mid": v(0, 174.25) * mm, "end": v(25, 149.25) * mm});
            skLineSegment(sketch, "E82", {"start": v(-25, 149.25) * mm, "end": v(-25, 127.08) * mm});
            skLineSegment(sketch, "E83", {"start": v(-25, 127.08) * mm, "end": v(-56.22, 74.25) * mm});
            skLineSegment(sketch, "E84", {"start": v(25, 149.25) * mm, "end": v(25, 127.08) * mm});
            skLineSegment(sketch, "E85", {"start": v(25, 127.08) * mm, "end": v(56.22, 74.25) * mm});
            skLineSegment(sketch, "E86", {"start": v(-74.25, 0) * mm, "end": v(74.25, 0) * mm, "construction": true});
            skLineSegment(sketch, "E87.MirrorCS", {"start": v(-25, -127.08) * mm, "end": v(-56.22, -74.25) * mm});
            skLineSegment(sketch, "E88.MirrorCS", {"start": v(-25, -149.25) * mm, "end": v(-25, -127.08) * mm});
            skArc(sketch, "E89.MirrorCS", {"start": v(-25, -149.25) * mm, "mid": v(0, -174.25) * mm, "end": v(25, -149.25) * mm});
            skLineSegment(sketch, "E90.MirrorCS", {"start": v(25, -149.25) * mm, "end": v(25, -127.08) * mm});
            skLineSegment(sketch, "E91.MirrorCS", {"start": v(25, -127.08) * mm, "end": v(56.22, -74.25) * mm});
            skCircle(sketch, "E92.MirrorC", {"center": v(0, -149.25) * mm, "radius": 10 * mm});
            skSolve(sketch);
        }
        {
            var Q0;
            Q0=makeQuery(id+"F16.imprint","IMPRINT",FACE,{"disambiguationData":[TD([[makeQuery(id+"F16.imprint","IMPRINT",EDGE,{"derivedFrom":sQuery(id+"F16.wireOp",EDGE,"E80")}),-1.0]])]});
            var Q1;
            {var subQ0=sQuery(id+"F16.wireOp",EDGE,"E87.MirrorCS");Q1=makeQuery(id+"F16.imprint","IMPRINT",FACE,{"disambiguationData":[TD([[makeQuery(id+"F16.imprint","IMPRINT",EDGE,{"derivedFrom":subQ0}),-1.0]])]});}
            var Q2;
            Q2=makeQuery(id+"F16.imprint","IMPRINT",FACE,{"disambiguationData":[TD([[makeQuery(id+"F16.imprint","IMPRINT",EDGE,{"derivedFrom":makeQuery(id+"F1.opExtrude","CAP_EDGE",EDGE,{"disambiguationData":[OSD([sQuery(id+"F0.wireOp",EDGE,"E1.left")])],"isStart":true})}),-1.0]])]});
            var Q3;
            Q3=makeQuery(id+"F2.opExtrude","CAP_FACE",FACE,{"disambiguationData":[OSD([sQuery(id+"F0.wireOp",EDGE,"E12"),sQuery(id+"F0.wireOp",EDGE,"E13"),sQuery(id+"F0.wireOp",EDGE,"E14"),sQuery(id+"F0.wireOp",EDGE,"E15"),sQuery(id+"F0.wireOp",EDGE,"E17.filletArc"),sQuery(id+"F0.wireOp",EDGE,"E18.filletArc"),sQuery(id+"F0.wireOp",EDGE,"E19.filletArc"),sQuery(id+"F0.wireOp",EDGE,"E20.filletArc"),sQuery(id+"F0.wireOp",EDGE,"E25.0"),sQuery(id+"F0.wireOp",EDGE,"E25.1"),sQuery(id+"F0.wireOp",EDGE,"E25.2"),sQuery(id+"F0.wireOp",EDGE,"E25.3"),sQuery(id+"F0.wireOp",EDGE,"E25.4"),sQuery(id+"F0.wireOp",EDGE,"E25.5"),sQuery(id+"F0.wireOp",EDGE,"E25.6"),sQuery(id+"F0.wireOp",EDGE,"E25.7")])],"isStart":false});
            extrude(context, id + "F17", {"entities" : qUnion([Q0, Q1, Q2]), "endBound" : BoundingType.UP_TO_SURFACE, "depth" : 10 * mm, "endBoundEntityFace" : qUnion([Q3]), "offsetDistance" : 25 * mm});
        }
    });
